# Revit family: NLRSen_AT_UN_RTFO_Return_Solid_Air
name_source: partatom
category: Air Terminals
revit_build: Autodesk Revit 2017 (Build: 20190508_0315(x64)
units: mm (PartAtom-declared; Revit-internal decimal feet)

## family parameters
Always vertical = Yes
Cut with Voids When Loaded = No
OmniClass Number = 23.75.70.21.27.11
OmniClass Title = Diffusers, Registers, and Grilles
Part Type = Normal
Room Calculation Point = Yes
Round Connector Dimension = Use Diameter
Shared = No
Work Plane-Based = No

## types (5) — shared parameters
Description = Round flanged Swirl return grill, Type RTFO
IfcDescription = Round flanged Swirl return grill, Type RTFO
IfcExportAs = IfcAirterminal
IfcExportType = Diffuser
Lookup_Article_Codes = Grill_Article_Codes
Lookup_Article_Data = RTFO_Article_Data_RT
Lookup_Article_Names = Grill_Article_Names
Lookup_Grill_Factors = Grill_Selection_Factors
Manufacturer = Solid Air Climate Solutions
Model = RTFO
NLRS_C_content_datum_uitgifte = 2019-10-01
NLRS_C_content_provider = Solid Air Climate Solutions
NLRS_C_content_versie = 2.03
NLRS_C_description = Round flanged Swirl return grill, Type RTFO
SACS_AX_Prefix = 822
SACS_Plenum_Material = Sendzimir verzinkt
SACS_Revised_ by = J. Feeke
SACS_Revision_Date = 2019-10-01
SACS_Revision_Number = 2.03
Type Comments = Please make sure flow is set to m3/h!
URL = https://solid-air.nl
zero-valued in all types: Cost

## per-type parameters (varying)
| type | Assembly Code | Max Flow | Min Flow | SACS_Base_Index | SACS_Plenum_A | SACS_Plenum_D1 | SACS_Plenum_D2 | SACS_Plenum_D2oval_H | SACS_Plenum_D2oval_W | SACS_Plenum_G | SACS_Plenum_H | SACS_Plenum_K | SACS_Plenum_Pmax | SACS_Plenum_Pmin | SACS_Plenum_Poval | SACS_Ring_Offset |
| 125 | 57.71 | 288 m³/h | 72 m³/h | 1 | 186 mm  [stored 0.610236 ft] | 123 mm  [stored 0.403543 ft] | 123 mm  [stored 0.403543 ft] | 73 mm  [stored 0.239501 ft] | 164 mm  [stored 0.538058 ft] | 171 mm  [stored 0.561024 ft] | 70 mm  [stored 0.229659 ft] | 35 mm  [stored 0.114829 ft] | 280 mm  [stored 0.918635 ft] | 260 mm  [stored 0.853018 ft] | 210 mm  [stored 0.688976 ft] | 59 mm |
| 160 | 57 | 450 m³/h | 108 m³/h | 2 | 221 mm  [stored 0.725066 ft] | 158 mm | 158 mm | 93 mm  [stored 0.305118 ft] | 208 mm | 206 mm  [stored 0.675853 ft] | 95 mm | 35 mm  [stored 0.114829 ft] | 305 mm  [stored 1.00066 ft] | 285 mm  [stored 0.935039 ft] | 220 mm  [stored 0.721785 ft] | 59 mm |
| 200 | 57 | 720 m³/h | 180 m³/h | 3 | 261 mm  [stored 0.856299 ft] | 200 mm  [stored 0.656168 ft] | 198 mm  [stored 0.649606 ft] | 117 mm  [stored 0.383858 ft] | 262 mm  [stored 0.85958 ft] | 245 mm  [stored 0.803806 ft] | 110 mm  [stored 0.360892 ft] | 45 mm  [stored 0.147638 ft] | 350 mm | 330 mm | 260 mm  [stored 0.853018 ft] | 69 mm  [stored 0.226378 ft] |
| 250 | 57 | 900 m³/h | 288 m³/h | 4 | 311 mm  [stored 1.02034 ft] | 250 mm  [stored 0.82021 ft] | 248 mm  [stored 0.813648 ft] | 117 mm  [stored 0.383858 ft] | 262 mm  [stored 0.85958 ft] | 296 mm  [stored 0.971129 ft] | 130 mm  [stored 0.426509 ft] | 55 mm  [stored 0.180446 ft] | 420 mm | 390 mm | 290 mm  [stored 0.951444 ft] | 79 mm |
| 315 | 57 | 900 m³/h | 288 m³/h | 5 | 376 mm | 315 mm | 313 mm  [stored 1.0269 ft] | 147 mm  [stored 0.482283 ft] | 330 mm | 361 mm | 135 mm  [stored 0.442913 ft] | 55 mm  [stored 0.180446 ft] | 490 mm | 460 mm | 335 mm | 79 mm |

note: [stored X ft] marks values corroborated as IEEE doubles in the binary element streams (Revit-internal decimal feet)

## geometry (parser evidence)
native form markers: Sweep x32
no freeform markers — native parametric forms only
